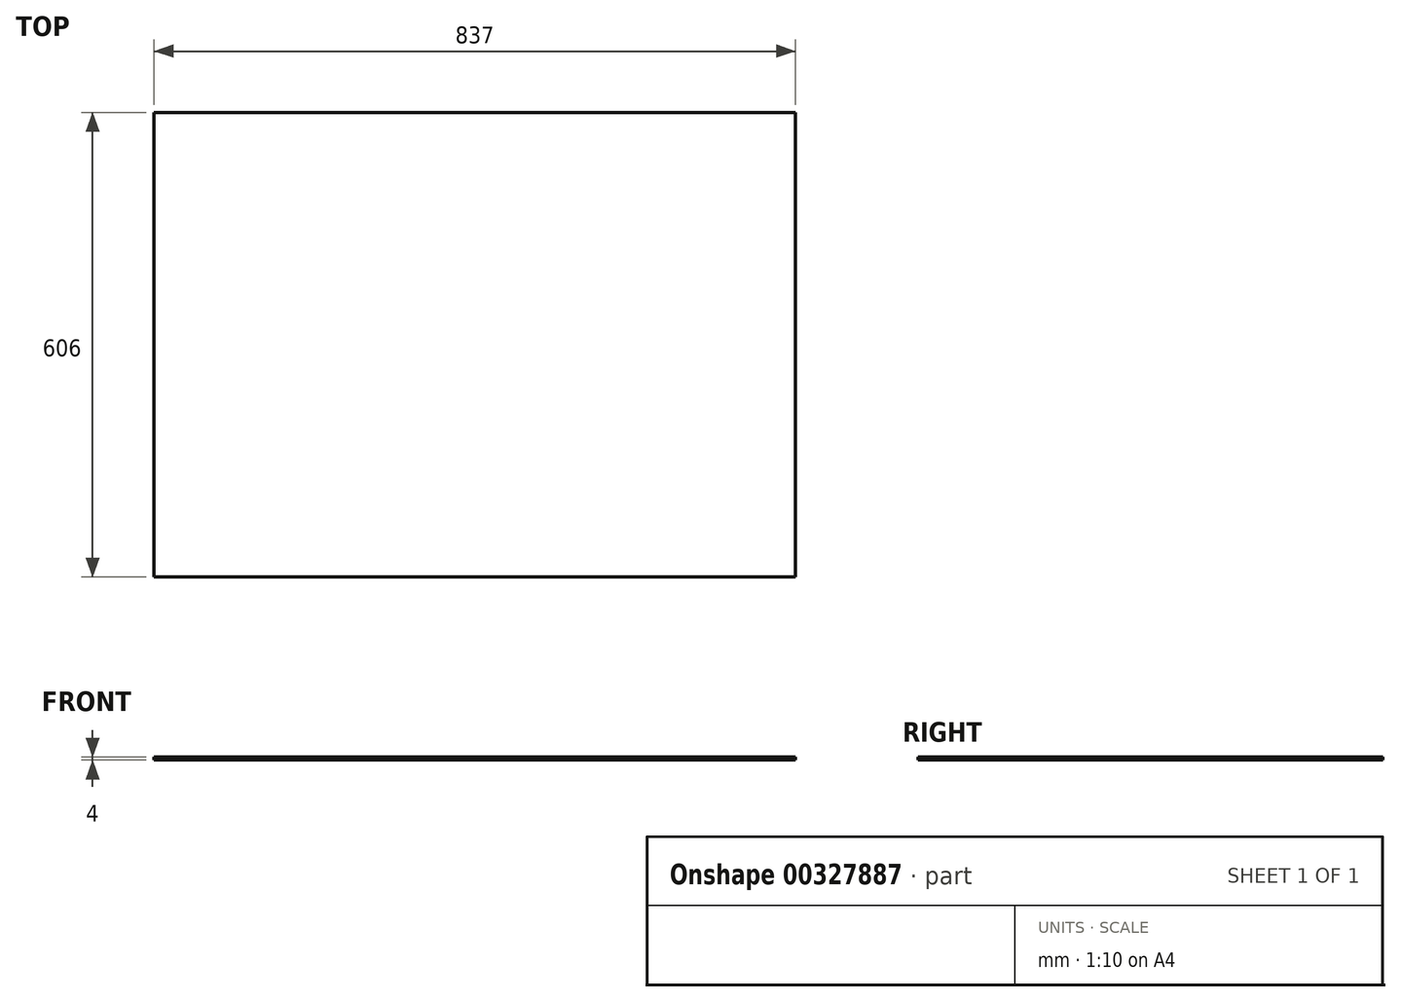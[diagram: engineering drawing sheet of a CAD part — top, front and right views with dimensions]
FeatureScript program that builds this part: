
annotation { "Feature Type Name" : "Feature", "Feature Type Description" : "" }
export const myFeature = defineFeature(function(context is Context, id is Id, definition is map)
    precondition{}
    {
        {
            var Q0;
            Q0=qCreatedBy(makeId("Top.planeOp"),FACE);
            var sketch = newSketch(context, id + "F0", { "sketchPlane" : qUnion([Q0])});
            skLineSegment(sketch, "E0.bottom", {"start": v(0, 0) * mm, "end": v(-837, 0) * mm});
            skLineSegment(sketch, "E0.top", {"start": v(0, 606) * mm, "end": v(-837, 606) * mm});
            skLineSegment(sketch, "E0.left", {"start": v(0, 0) * mm, "end": v(0, 606) * mm});
            skLineSegment(sketch, "E0.right", {"start": v(-837, 0) * mm, "end": v(-837, 606) * mm});
            skSolve(sketch);
        }
        {
            var Q0;
            Q0 = qSketchRegion(id + "F0", true);
            extrude(context, id + "F1", {"entities" : qUnion([Q0]), "depth" : 4 * mm});
        }
    });
